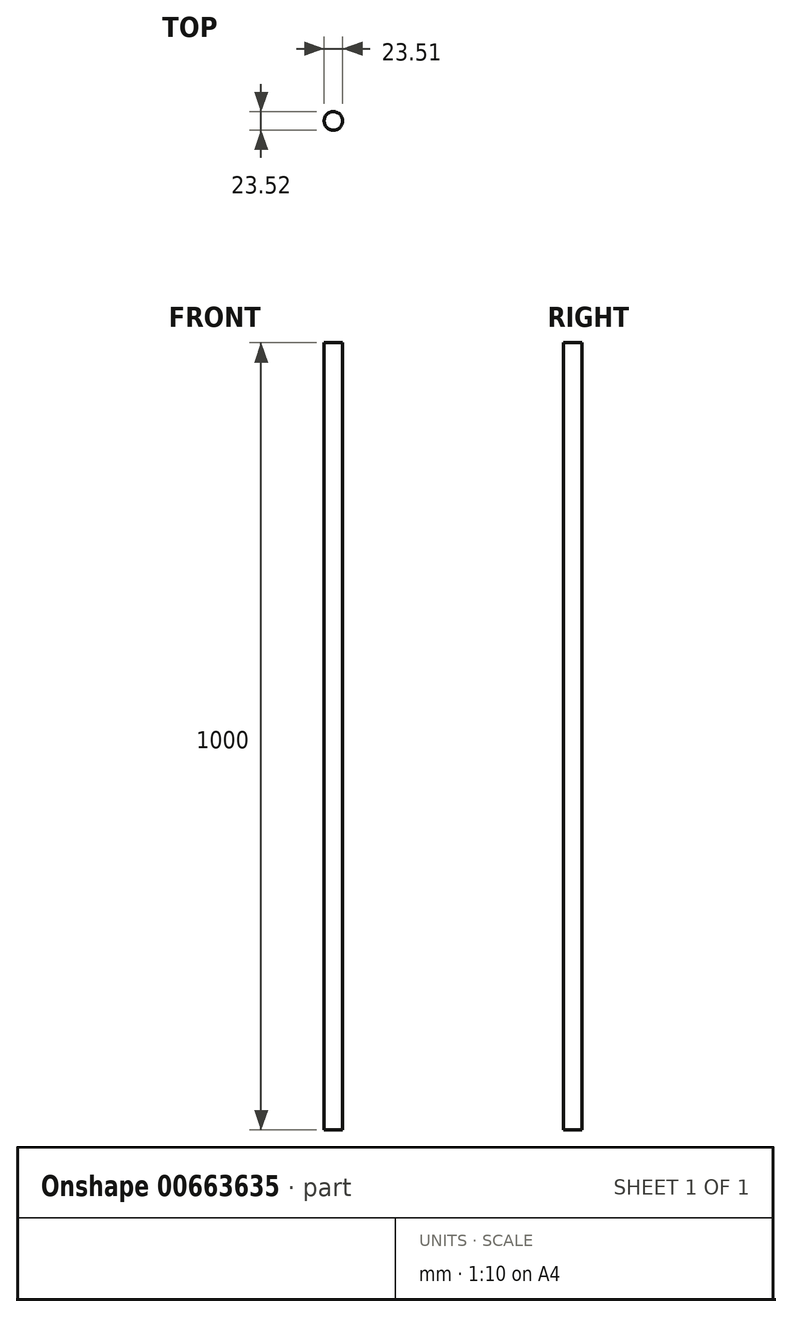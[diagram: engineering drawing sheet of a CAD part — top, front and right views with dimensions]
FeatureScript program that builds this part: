
annotation { "Feature Type Name" : "Feature", "Feature Type Description" : "" }
export const myFeature = defineFeature(function(context is Context, id is Id, definition is map)
    precondition{}
    {
        {
            var Q0;
            Q0=qCreatedBy(makeId("Top.planeOp"),FACE);
            var sketch = newSketch(context, id + "F0", { "sketchPlane" : qUnion([Q0])});
            skCircle(sketch, "E0", {"center": v(-17.2, 3.71) * mm, "radius": 11.76 * mm});
            skSolve(sketch);
        }
        {
            var Q0;
            Q0 = qSketchRegion(id + "F0", true);
            extrude(context, id + "F1", {"entities" : qUnion([Q0]), "depth" : 1000 * mm, "offsetDistance" : 25.4 * mm});
        }
    });
